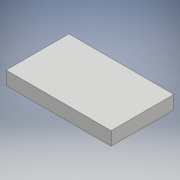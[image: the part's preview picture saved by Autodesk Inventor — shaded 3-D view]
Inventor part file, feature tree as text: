
AUTODESK INVENTOR PART (.ipt)
format: ipt  version: 2017 (Build 210142000, 142)  size: 88,576 bytes
history: native  units: mm
features: extrude x1, sketch x1
ambient origin geometry x8: Origin, YZ Plane, XZ Plane, XY Plane, X Axis, Y Axis, Z Axis, Center Point
bodies: Solid1 (feature_tree)
feature tree (2):
  extrude  "Extrusion1"  Depth=2800.0mm
  sketch  "Sketch1"  dims[d0=4680.0mm d1=2800.0mm d2=600.0mm d3=0.0mm]
